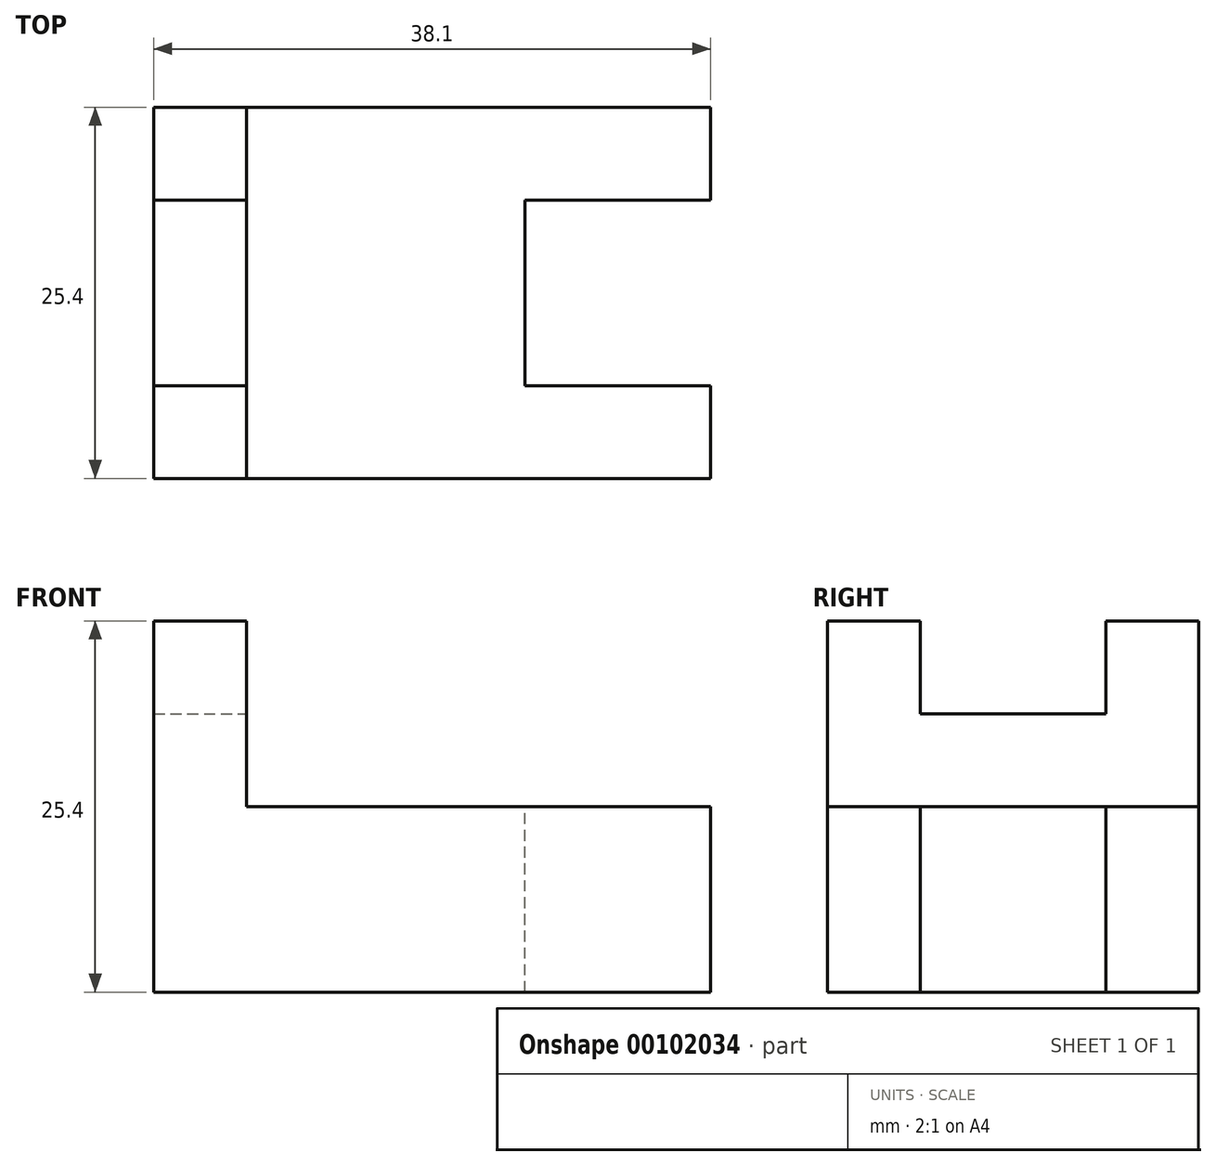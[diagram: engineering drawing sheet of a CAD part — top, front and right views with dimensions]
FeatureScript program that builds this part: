
annotation { "Feature Type Name" : "Feature", "Feature Type Description" : "" }
export const myFeature = defineFeature(function(context is Context, id is Id, definition is map)
    precondition{}
    {
        {
            var Q0;
            Q0=qCreatedBy(makeId("Front.planeOp"),FACE);
            var sketch = newSketch(context, id + "F0", { "sketchPlane" : qUnion([Q0])});
            skLineSegment(sketch, "E0", {"start": v(0, 0) * mm, "end": v(0, 25.4) * mm});
            skLineSegment(sketch, "E1", {"start": v(0, 25.4) * mm, "end": v(6.35, 25.4) * mm});
            skLineSegment(sketch, "E2", {"start": v(6.35, 25.4) * mm, "end": v(6.35, 12.7) * mm});
            skLineSegment(sketch, "E3", {"start": v(6.35, 12.7) * mm, "end": v(38.1, 12.7) * mm});
            skLineSegment(sketch, "E4", {"start": v(38.1, 12.7) * mm, "end": v(38.1, 0) * mm});
            skLineSegment(sketch, "E5", {"start": v(38.1, 0) * mm, "end": v(0, 0) * mm});
            skSolve(sketch);
        }
        {
            var Q0;
            Q0 = qSketchRegion(id + "F0", true);
            extrude(context, id + "F1", {"entities" : qUnion([Q0]), "depth" : 25.4 * mm});
        }
        {
            var Q0;
            Q0=makeQuery(id+"F1.opExtrude","SWEPT_FACE",FACE,{"disambiguationData":[OSD([sQuery(id+"F0.wireOp",EDGE,"E3")])]});
            var sketch = newSketch(context, id + "F2", { "sketchPlane" : qUnion([Q0])});
            skLineSegment(sketch, "E6.bottom", {"start": v(38.1, -19.05) * mm, "end": v(25.4, -19.05) * mm});
            skLineSegment(sketch, "E6.top", {"start": v(38.1, -6.35) * mm, "end": v(25.4, -6.35) * mm});
            skLineSegment(sketch, "E6.left", {"start": v(38.1, -19.05) * mm, "end": v(38.1, -6.35) * mm});
            skLineSegment(sketch, "E6.right", {"start": v(25.4, -19.05) * mm, "end": v(25.4, -6.35) * mm});
            skSolve(sketch);
        }
        {
            var Q0;
            Q0=makeQuery(id+"F2.imprint","IMPRINT",FACE,{"disambiguationData":[TD([[makeQuery(id+"F2.imprint","IMPRINT",EDGE,{"derivedFrom":sQuery(id+"F2.wireOp",EDGE,"E6.bottom")}),-1.0]])]});
            extrude(context, id + "F3", {"entities" : qUnion([Q0]), "operationType" : NewBodyOperationType.REMOVE, "endBound" : BoundingType.THROUGH_ALL, "oppositeDirection" : true, "depth" : 25.4 * mm});
        }
        {
            var Q0;
            Q0=makeQuery(id+"F1.opExtrude","SWEPT_FACE",FACE,{"disambiguationData":[OSD([sQuery(id+"F0.wireOp",EDGE,"E2")])]});
            var sketch = newSketch(context, id + "F4", { "sketchPlane" : qUnion([Q0])});
            skLineSegment(sketch, "E7.bottom", {"start": v(-19.05, 25.4) * mm, "end": v(-6.35, 25.4) * mm});
            skLineSegment(sketch, "E7.top", {"start": v(-19.05, 19.05) * mm, "end": v(-6.35, 19.05) * mm});
            skLineSegment(sketch, "E7.left", {"start": v(-19.05, 25.4) * mm, "end": v(-19.05, 19.05) * mm});
            skLineSegment(sketch, "E7.right", {"start": v(-6.35, 25.4) * mm, "end": v(-6.35, 19.05) * mm});
            skSolve(sketch);
        }
        {
            var Q0;
            Q0=makeQuery(id+"F4.imprint","IMPRINT",FACE,{"disambiguationData":[TD([[makeQuery(id+"F4.imprint","IMPRINT",EDGE,{"derivedFrom":sQuery(id+"F4.wireOp",EDGE,"E7.bottom")}),-1.0]])]});
            extrude(context, id + "F5", {"entities" : qUnion([Q0]), "operationType" : NewBodyOperationType.REMOVE, "endBound" : BoundingType.THROUGH_ALL, "oppositeDirection" : true, "depth" : 25.4 * mm});
        }
    });
